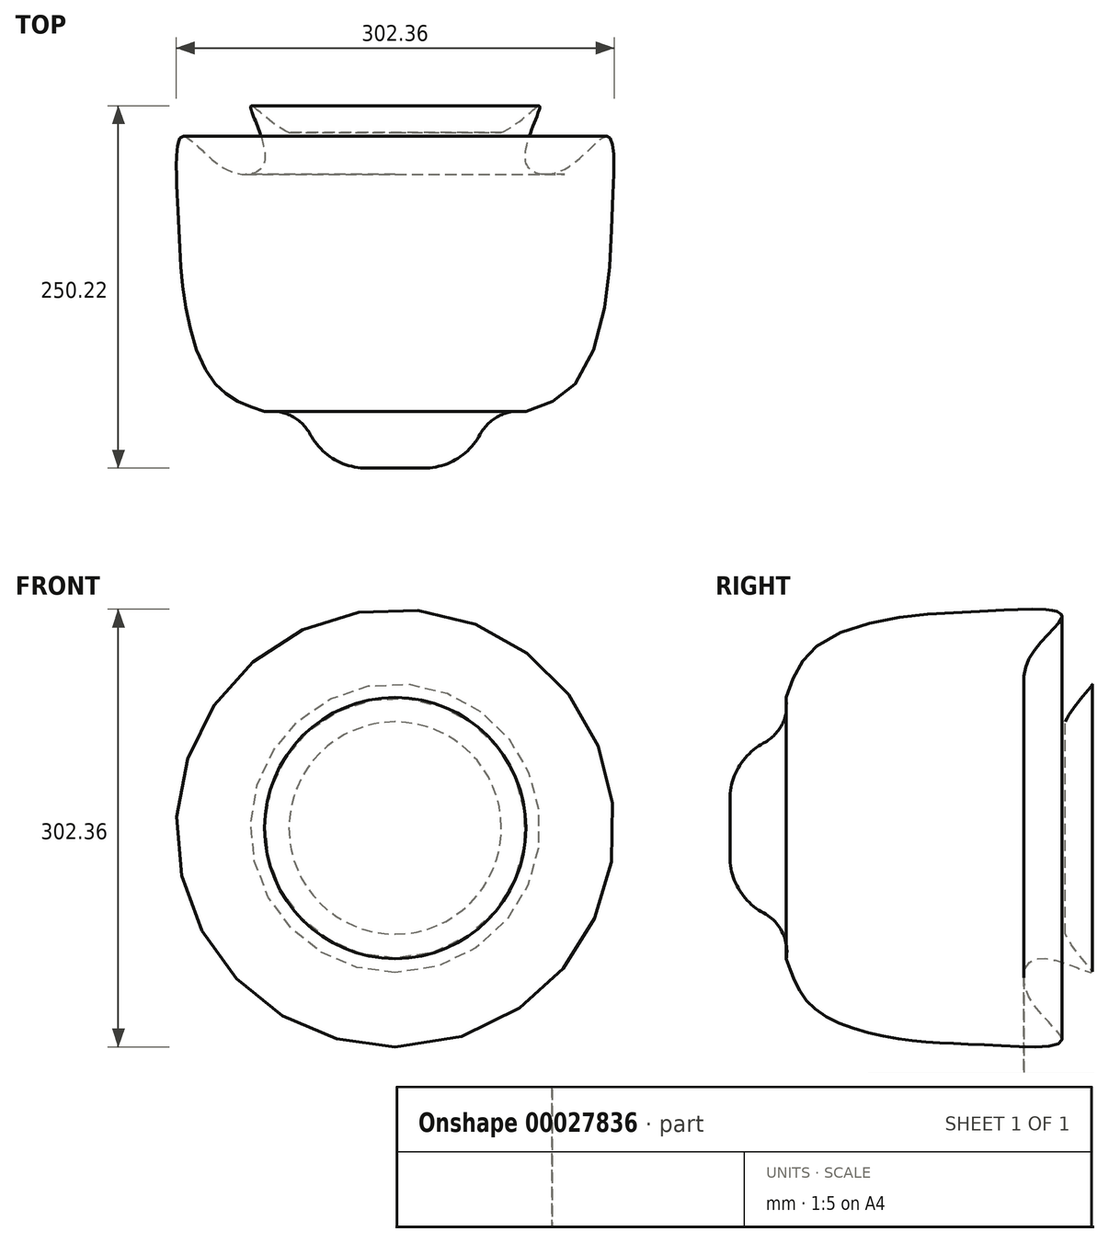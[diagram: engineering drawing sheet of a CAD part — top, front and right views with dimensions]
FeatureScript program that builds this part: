
annotation { "Feature Type Name" : "Feature", "Feature Type Description" : "" }
export const myFeature = defineFeature(function(context is Context, id is Id, definition is map)
    precondition{}
    {
        {
            var Q0;
            Q0=qCreatedBy(makeId("Top.planeOp"),FACE);
            var sketch = newSketch(context, id + "F0", { "sketchPlane" : qUnion([Q0])});
            skLineSegment(sketch, "E0", {"start": v(0, -107.06) * mm, "end": v(0, 124.65) * mm});
            skLineSegment(sketch, "E1", {"start": v(0, -107.06) * mm, "end": v(-19.77, -107.06) * mm});
            skArc(sketch, "E2", {"start": v(-19.77, -107.06) * mm, "mid": v(-42.49, -100.77) * mm, "end": v(-58.74, -83.7) * mm});
            skArc(sketch, "E3", {"start": v(-58.74, -83.7) * mm, "mid": v(-72, -70.84) * mm, "end": v(-90.26, -68.06) * mm});
            skFitSpline(sketch, "E4", {"points": [v(-90.26, -68.06) * mm, v(-124.55, -48.65) * mm, v(-145.66, 9.9) * mm, v(-149.84, 70.45) * mm, v(-147.06, 122.08) * mm, v(-116.95, 99.54) * mm, v(-90.26, 104.47) * mm, v(-99.8, 142.85) * mm, v(-73.35, 124.65) * mm], "startDerivative": vector(-311.97, 105.54) * mm, "endDerivative": vector(378, -178.09) * mm});
            skLineSegment(sketch, "E5", {"start": v(-73.35, 124.65) * mm, "end": v(0, 124.65) * mm});
            skSolve(sketch);
        }
        {
            var Q0;
            Q0=makeQuery(id+"F0.imprint","IMPRINT",FACE,{"disambiguationData":[TD([[makeQuery(id+"F0.imprint","IMPRINT",EDGE,{"derivedFrom":sQuery(id+"F0.wireOp",EDGE,"E0")}),1.0]])]});
            var Q1;
            Q1=sQuery(id+"F0.wireOp",EDGE,"E0");
            revolve(context, id + "F1", {"entities" : qUnion([Q0]), "axis" : qUnion([Q1]), "revolveType" : RevolveType.FULL});
        }
    });
